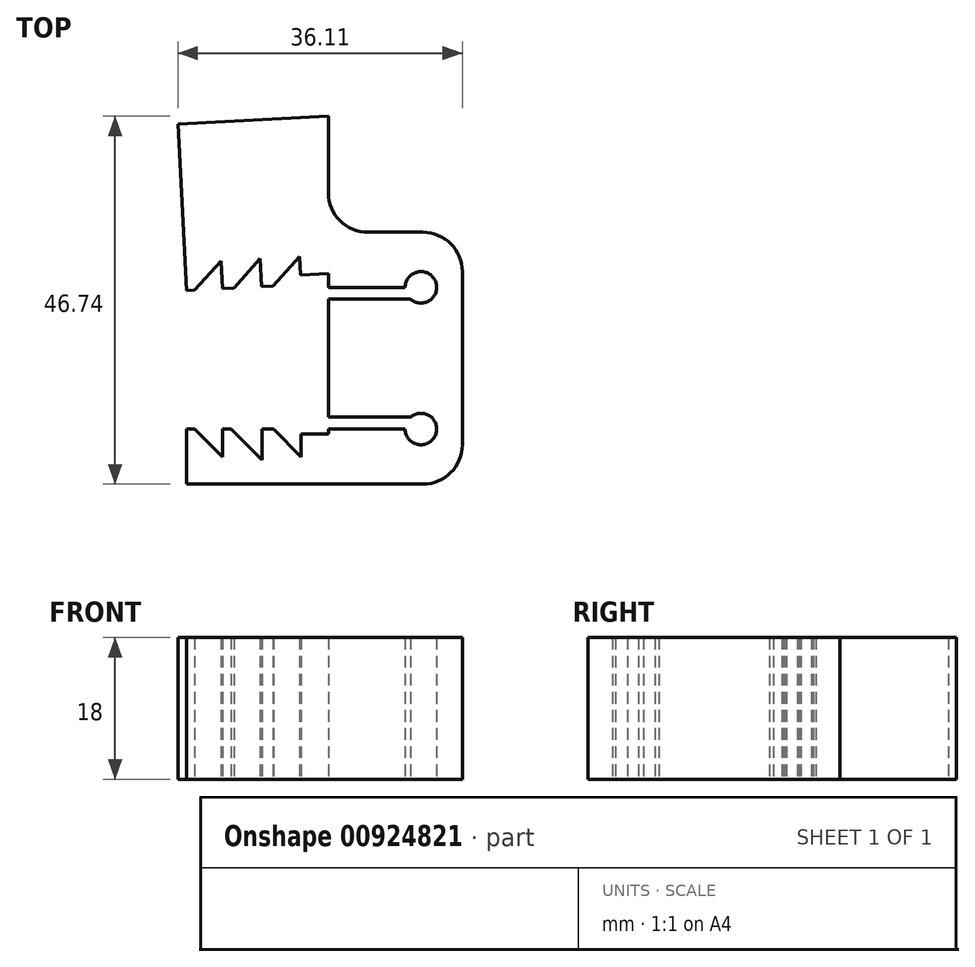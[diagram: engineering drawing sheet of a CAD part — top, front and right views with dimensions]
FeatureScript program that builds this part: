
annotation { "Feature Type Name" : "Feature", "Feature Type Description" : "" }
export const myFeature = defineFeature(function(context is Context, id is Id, definition is map)
    precondition{}
    {
        {
            var Q0;
            Q0=qCreatedBy(makeId("Top.planeOp"),FACE);
            var sketch = newSketch(context, id + "F0", { "sketchPlane" : qUnion([Q0])});
            skLineSegment(sketch, "E0.bottom", {"start": v(-9.38, 9.88) * mm, "end": v(8.62, 10.82) * mm});
            skLineSegment(sketch, "E0.top", {"start": v(-9.38, -7.72) * mm, "end": v(8.62, -7.72) * mm});
            skLineSegment(sketch, "E0.left", {"start": v(-9.38, 10.28) * mm, "end": v(-9.38, -7.72) * mm});
            skLineSegment(sketch, "E0.right", {"start": v(8.62, 10.28) * mm, "end": v(8.62, -7.72) * mm});
            skLineSegment(sketch, "E1", {"start": v(-9.38, 9.88) * mm, "end": v(-9.38, 17.28) * mm});
            skLineSegment(sketch, "E2", {"start": v(-9.38, 17.28) * mm, "end": v(25.62, 17.28) * mm});
            skLineSegment(sketch, "E3", {"start": v(25.62, 17.28) * mm, "end": v(25.62, -14.72) * mm});
            skLineSegment(sketch, "E4", {"start": v(25.62, -14.72) * mm, "end": v(-9.38, -14.72) * mm});
            skLineSegment(sketch, "E5", {"start": v(-9.38, -14.72) * mm, "end": v(-9.38, -7.72) * mm});
            skCircle(sketch, "E6", {"center": v(20.37, 10.28) * mm, "radius": 2 * mm});
            skCircle(sketch, "E7", {"center": v(20.37, -7.72) * mm, "radius": 2 * mm});
            skLineSegment(sketch, "E8", {"start": v(8.62, 1.28) * mm, "end": v(21.35, 1.28) * mm, "construction": true});
            skLineSegment(sketch, "E9", {"start": v(-8.38, -7.72) * mm, "end": v(-4.85, -11.26) * mm});
            skLineSegment(sketch, "E10", {"start": v(-4.85, -11.26) * mm, "end": v(-4.85, -7.72) * mm});
            skLineSegment(sketch, "E11.MirrorCS", {"start": v(-5.04, 13.65) * mm, "end": v(-4.85, 10.11) * mm});
            skLineSegment(sketch, "E12.MirrorCS", {"start": v(-8.38, 9.93) * mm, "end": v(-5.04, 13.65) * mm});
            skLineSegment(sketch, "E13.1.0.0", {"start": v(-0.04, 13.9) * mm, "end": v(0.18, 9.67) * mm});
            skLineSegment(sketch, "E13.1.0.1", {"start": v(-3.67, 9.88) * mm, "end": v(-0.04, 13.9) * mm});
            skLineSegment(sketch, "E13.1.0.2", {"start": v(-3.78, -7.72) * mm, "end": v(0.15, -11.66) * mm});
            skLineSegment(sketch, "E13.1.0.3", {"start": v(0.15, -11.66) * mm, "end": v(0.15, -7.72) * mm});
            skLineSegment(sketch, "E13.2.0.0", {"start": v(4.95, 14.57) * mm, "end": v(5.13, 11.04) * mm});
            skLineSegment(sketch, "E13.2.0.1", {"start": v(1.6, 10.45) * mm, "end": v(4.97, 14.2) * mm});
            skLineSegment(sketch, "E13.2.0.2", {"start": v(1.62, -7.72) * mm, "end": v(5.15, -11.26) * mm});
            skLineSegment(sketch, "E13.2.0.3", {"start": v(5.15, -11.26) * mm, "end": v(5.15, -7.72) * mm});
            skLineSegment(sketch, "E13.direction1", {"start": v(-4.85, 9.88) * mm, "end": v(0.15, 9.88) * mm, "construction": true});
            skLineSegment(sketch, "E14", {"start": v(8.62, 10.28) * mm, "end": v(18.37, 10.28) * mm});
            skLineSegment(sketch, "E15", {"start": v(8.62, -7.72) * mm, "end": v(18.37, -7.72) * mm});
            skLineSegment(sketch, "E16", {"start": v(8.62, -6.22) * mm, "end": v(20.37, -6.22) * mm});
            skLineSegment(sketch, "E17", {"start": v(-9.38, 17.28) * mm, "end": v(-9.38, 28.28) * mm});
            skLineSegment(sketch, "E18", {"start": v(-9.38, 28.28) * mm, "end": v(8.62, 28.28) * mm});
            skLineSegment(sketch, "E19", {"start": v(8.62, 28.28) * mm, "end": v(8.62, 17.28) * mm});
            skLineSegment(sketch, "E20", {"start": v(8.62, 8.78) * mm, "end": v(20.37, 8.78) * mm});
            skLineSegment(sketch, "E21", {"start": v(5.1, 11.84) * mm, "end": v(8.62, 12.02) * mm});
            skLineSegment(sketch, "E22", {"start": v(8.62, 12.02) * mm, "end": v(8.62, 10.28) * mm});
            skLineSegment(sketch, "E23", {"start": v(5.15, -8.36) * mm, "end": v(8.62, -8.36) * mm});
            skLineSegment(sketch, "E24", {"start": v(8.62, -8.36) * mm, "end": v(8.62, -7.72) * mm});
            skLineSegment(sketch, "E25", {"start": v(-9.38, 9.88) * mm, "end": v(-10.5, 31.02) * mm});
            skLineSegment(sketch, "E26", {"start": v(-10.5, 31.02) * mm, "end": v(8.62, 32.02) * mm});
            skLineSegment(sketch, "E27", {"start": v(8.62, 32.02) * mm, "end": v(8.62, 28.28) * mm});
            skSolve(sketch);
        }
        {
            var Q0;
            {var subQ0=sQuery(id+"F0.wireOp",EDGE,"E17");Q0=makeQuery(id+"F0.imprint","IMPRINT",FACE,{"disambiguationData":[TD([[makeQuery(id+"F0.imprint","IMPRINT",EDGE,{"derivedFrom":subQ0}),-1.0]])]});}
            var Q1;
            {var subQ5=sQuery(id+"F0.wireOp",EDGE,"E1");Q1=makeQuery(id+"F0.imprint","IMPRINT",FACE,{"disambiguationData":[TD([[makeQuery(id+"F0.imprint","IMPRINT",EDGE,{"derivedFrom":subQ5}),-1.0]])]});}
            var Q2;
            {var subQ0=sQuery(id+"F0.wireOp",EDGE,"E17");Q2=makeQuery(id+"F0.imprint","IMPRINT",FACE,{"disambiguationData":[TD([[makeQuery(id+"F0.imprint","IMPRINT",EDGE,{"derivedFrom":subQ0}),1.0]])]});}
            extrude(context, id + "F1", {"entities" : qUnion([Q0, Q1, Q2]), "depth" : 18 * mm, "offsetDistance" : 25 * mm});
        }
        {
            var Q0;
            Q0=makeQuery(id+"F1.opExtrude","SWEPT_EDGE",EDGE,{"disambiguationData":[OSD([sQuery(id+"F0.wireOp",EDGE,"E2"),sQuery(id+"F0.wireOp",EDGE,"E19")])]});
            var Q1;
            Q1=makeQuery(id+"F1.opExtrude","SWEPT_EDGE",EDGE,{"disambiguationData":[OSD([sQuery(id+"F0.wireOp",EDGE,"E2"),sQuery(id+"F0.wireOp",EDGE,"E3")])]});
            var Q2;
            Q2=makeQuery(id+"F1.opExtrude","SWEPT_EDGE",EDGE,{"disambiguationData":[OSD([sQuery(id+"F0.wireOp",EDGE,"E3"),sQuery(id+"F0.wireOp",EDGE,"E4")])]});
            fillet(context, id + "F2", {"entities" : qUnion([Q0, Q1, Q2]), "radius" : 5 * mm, "tangentPropagation" : true, "allowEdgeOverflow" : false});
        }
    });
